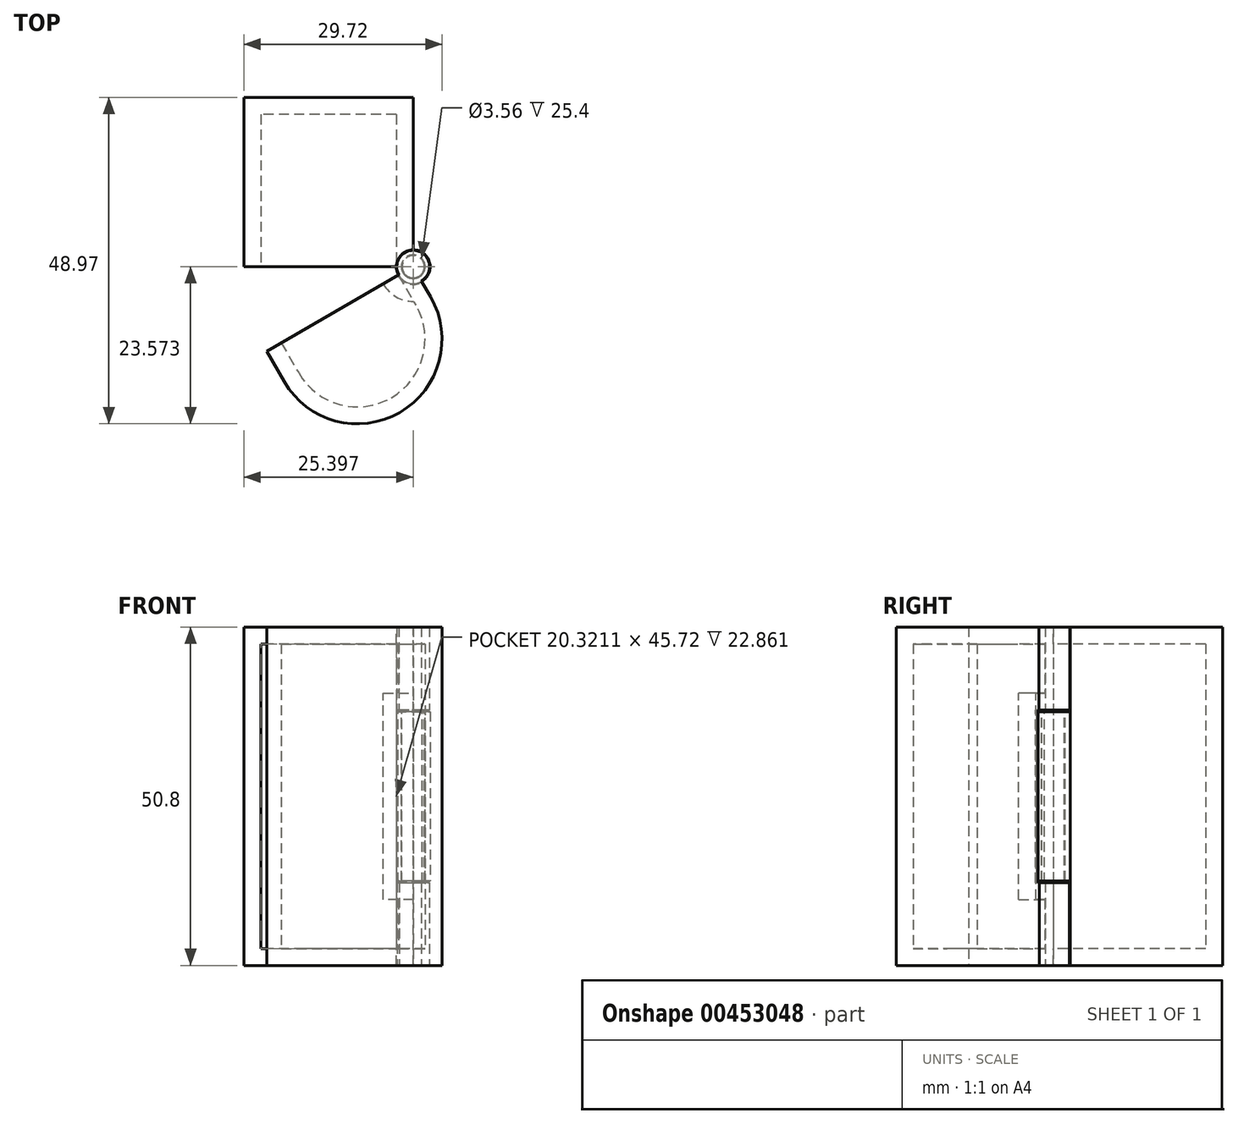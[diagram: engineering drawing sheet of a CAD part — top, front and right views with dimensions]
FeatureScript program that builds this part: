
annotation { "Feature Type Name" : "Feature", "Feature Type Description" : "" }
export const myFeature = defineFeature(function(context is Context, id is Id, definition is map)
    precondition{}
    {
        {
            var Q0;
            Q0=qCreatedBy(makeId("Top.planeOp"),FACE);
            var sketch = newSketch(context, id + "F0", { "sketchPlane" : qUnion([Q0])});
            skLineSegment(sketch, "E0.bottom", {"start": v(-18.17, 30.36) * mm, "end": v(-43.57, 30.36) * mm});
            skLineSegment(sketch, "E0.top", {"start": v(-18.17, 4.96) * mm, "end": v(-43.57, 4.96) * mm});
            skLineSegment(sketch, "E0.left", {"start": v(-18.17, 30.36) * mm, "end": v(-18.17, 4.96) * mm});
            skLineSegment(sketch, "E0.right", {"start": v(-43.57, 30.36) * mm, "end": v(-43.57, 4.96) * mm});
            skSolve(sketch);
        }
        {
            var Q0;
            Q0=makeQuery(id+"F0.imprint","IMPRINT",FACE,{"disambiguationData":[TD([[makeQuery(id+"F0.imprint","IMPRINT",EDGE,{"derivedFrom":sQuery(id+"F0.wireOp",EDGE,"E0.bottom")}),1.0]])]});
            extrude(context, id + "F1", {"entities" : qUnion([Q0]), "depth" : 50.8 * mm});
        }
        {
            var Q0;
            Q0=makeQuery(id+"F1.opExtrude","SWEPT_FACE",FACE,{"disambiguationData":[OSD([sQuery(id+"F0.wireOp",EDGE,"E0.top")])]});
            shell(context, id + "F2", {"entities" : qUnion([Q0]), "thickness" : 2.54 * mm});
        }
        {
            var Q0;
            Q0=makeQuery(id+"F1.opExtrude","SWEPT_FACE",FACE,{"disambiguationData":[OSD([sQuery(id+"F0.wireOp",EDGE,"E0.top")])]});
            var sketch = newSketch(context, id + "F3", { "sketchPlane" : qUnion([Q0])});
            skLineSegment(sketch, "E1", {"start": v(-20.71, 48.26) * mm, "end": v(-20.71, 50.8) * mm});
            skLineSegment(sketch, "E2", {"start": v(-20.71, 50.8) * mm, "end": v(-20.71, 0) * mm});
            skSolve(sketch);
        }
        {
            var Q0;
            {var subQ0=sQuery(id+"F0.wireOp",EDGE,"E0.top");var subQ1=makeQuery(id+"F1.opExtrude","SWEPT_EDGE",EDGE,{"disambiguationData":[OSD([subQ0,sQuery(id+"F0.wireOp",EDGE,"E0.left")])]});Q0=makeQuery(id+"F3.imprint","IMPRINT",FACE,{"disambiguationData":[TD([[makeQuery(id+"F3.imprint","IMPRINT",EDGE,{"derivedFrom":subQ1}),-1.0]])]});}
            var Q1;
            Q1=makeQuery(id+"F1.opExtrude","SWEPT_EDGE",EDGE,{"disambiguationData":[OSD([sQuery(id+"F0.wireOp",EDGE,"E0.top"),sQuery(id+"F0.wireOp",EDGE,"E0.left")])]});
            revolve(context, id + "F4", {"operationType" : NewBodyOperationType.ADD, "entities" : qUnion([Q0]), "axis" : qUnion([Q1]), "revolveType" : RevolveType.ONE_DIRECTION, "oppositeDirection" : true, "angle" : 270 * degree});
        }
        {
            var Q0;
            {var subQ0=sQuery(id+"F0.wireOp",EDGE,"E0.top");var subQ1=makeQuery(id+"F1.opExtrude","CAP_EDGE",EDGE,{"disambiguationData":[OSD([subQ0])],"isStart":false});var subQ2=sQuery(id+"F0.wireOp",EDGE,"E0.left");Q0=makeQuery(id+"F4.boolean.opBoolean","MERGE",FACE,{"derivedFrom":[makeQuery(id+"F1.opExtrude","CAP_FACE",FACE,{"disambiguationData":[OSD([sQuery(id+"F0.wireOp",EDGE,"E0.bottom"),subQ0,subQ2,sQuery(id+"F0.wireOp",EDGE,"E0.right")])],"isStart":false}),makeQuery(id+"F4.opRevolve","SWEPT_FACE",FACE,{"disambiguationData":[OSD([subQ0]),TDD([makeQuery(id+"F3.imprint","IMPRINT",EDGE,{"disambiguationData":[TD([[makeQuery(id+"F3.imprint","INTERSECT",VERTEX,{"derivedFrom":[subQ1,sQuery(id+"F3.wireOp",EDGE,"E2")]}),1.0]])],"derivedFrom":subQ1})])]})]});}
            var sketch = newSketch(context, id + "F5", { "sketchPlane" : qUnion([Q0])});
            skCircle(sketch, "E3", {"center": v(-18.17, 4.96) * mm, "radius": 2.54 * mm});
            skSolve(sketch);
        }
        {
            var Q0;
            {var subQ0=sQuery(id+"F0.wireOp",EDGE,"E0.top");var subQ1=makeQuery(id+"F1.opExtrude","CAP_EDGE",EDGE,{"disambiguationData":[OSD([subQ0])],"isStart":true});var subQ2=sQuery(id+"F0.wireOp",EDGE,"E0.left");Q0=makeQuery(id+"F4.boolean.opBoolean","MERGE",FACE,{"derivedFrom":[makeQuery(id+"F1.opExtrude","CAP_FACE",FACE,{"disambiguationData":[OSD([sQuery(id+"F0.wireOp",EDGE,"E0.bottom"),subQ0,subQ2,sQuery(id+"F0.wireOp",EDGE,"E0.right")])],"isStart":true}),makeQuery(id+"F4.opRevolve","SWEPT_FACE",FACE,{"disambiguationData":[OSD([subQ0]),TDD([makeQuery(id+"F3.imprint","IMPRINT",EDGE,{"disambiguationData":[TD([[makeQuery(id+"F3.imprint","INTERSECT",VERTEX,{"derivedFrom":[subQ1,sQuery(id+"F3.wireOp",EDGE,"E2")]}),1.0]])],"derivedFrom":subQ1})])]})]});}
            var sketch = newSketch(context, id + "F6", { "sketchPlane" : qUnion([Q0])});
            skCircle(sketch, "E4", {"center": v(-18.17, -4.96) * mm, "radius": 2.54 * mm});
            skSolve(sketch);
        }
        {
            var Q0;
            {var subQ0=sQuery(id+"F6.wireOp",EDGE,"E4");var subQ1=makeQuery(id+"F6.imprint","INTERSECT",VERTEX,{"derivedFrom":[makeQuery(id+"F1.opExtrude","CAP_EDGE",EDGE,{"disambiguationData":[OSD([sQuery(id+"F0.wireOp",EDGE,"E0.top")])],"isStart":true}),subQ0]});Q0=makeQuery(id+"F6.imprint","IMPRINT",FACE,{"disambiguationData":[TD([[makeQuery(id+"F6.imprint","IMPRINT",EDGE,{"disambiguationData":[TD([[subQ1,1.0]])],"derivedFrom":subQ0}),1.0]])]});}
            extrude(context, id + "F7", {"entities" : qUnion([Q0]), "operationType" : NewBodyOperationType.REMOVE, "oppositeDirection" : true, "depth" : 12.7 * mm});
        }
        {
            var Q0;
            {var subQ0=sQuery(id+"F5.wireOp",EDGE,"E3");Q0=makeQuery(id+"F5.imprint","IMPRINT",FACE,{"disambiguationData":[TD([[makeQuery(id+"F5.imprint","IMPRINT",EDGE,{"disambiguationData":[OD(0.0)],"derivedFrom":subQ0}),1.0]])]});}
            var sketch = newSketch(context, id + "F8", { "sketchPlane" : qUnion([Q0])});
            skArc(sketch, "E5.0", {"start": v(-19.95, 4.96) * mm, "mid": v(-16.92, 3.7) * mm, "end": v(-18.17, 6.74) * mm});
            skArc(sketch, "E5.1", {"start": v(-18.17, 6.74) * mm, "mid": v(-19.43, 6.22) * mm, "end": v(-19.95, 4.96) * mm});
            skSolve(sketch);
        }
        {
            var Q0;
            Q0=makeQuery(id+"F8.imprint","IMPRINT",FACE,{"disambiguationData":[TD([[makeQuery(id+"F8.imprint","IMPRINT",EDGE,{"derivedFrom":sQuery(id+"F8.wireOp",EDGE,"E5.0")}),1.0]])]});
            extrude(context, id + "F9", {"entities" : qUnion([Q0]), "operationType" : NewBodyOperationType.REMOVE, "endBound" : BoundingType.UP_TO_NEXT, "oppositeDirection" : true, "depth" : 25.4 * mm});
        }
        {
            var Q0;
            {var subQ0=sQuery(id+"F5.wireOp",EDGE,"E3");Q0=makeQuery(id+"F5.imprint","IMPRINT",FACE,{"disambiguationData":[TD([[makeQuery(id+"F5.imprint","IMPRINT",EDGE,{"disambiguationData":[OD(0.0)],"derivedFrom":subQ0}),1.0]])]});}
            extrude(context, id + "F10", {"entities" : qUnion([Q0]), "operationType" : NewBodyOperationType.REMOVE, "oppositeDirection" : true, "depth" : 12.7 * mm});
        }
        {
            var Q0;
            Q0=qCreatedBy(makeId("Top.planeOp"),FACE);
            var sketch = newSketch(context, id + "F11", { "sketchPlane" : qUnion([Q0])});
            skLineSegment(sketch, "E6.bottom", {"start": v(-43.63, 4.5) * mm, "end": v(-18.25, 4.5) * mm});
            skLineSegment(sketch, "E6.top", {"start": v(-43.63, -13.44) * mm, "end": v(-18.25, -13.44) * mm});
            skLineSegment(sketch, "E6.left", {"start": v(-43.63, 4.5) * mm, "end": v(-43.63, -13.44) * mm});
            skLineSegment(sketch, "E6.right", {"start": v(-18.25, 4.5) * mm, "end": v(-18.25, -13.44) * mm});
            skSolve(sketch);
        }
        {
            var Q0;
            Q0=makeQuery(id+"F11.imprint","IMPRINT",FACE,{"disambiguationData":[TD([[makeQuery(id+"F11.imprint","IMPRINT",EDGE,{"derivedFrom":sQuery(id+"F11.wireOp",EDGE,"E6.bottom")}),-1.0]])]});
            extrude(context, id + "F12", {"entities" : qUnion([Q0]), "depth" : 12.45 * mm});
        }
        {
            var Q0;
            Q0=makeQuery(id+"F12.opExtrude","SWEPT_BODY",BODY,{"disambiguationData":[OSD([sQuery(id+"F11.wireOp",EDGE,"E6.bottom"),sQuery(id+"F11.wireOp",EDGE,"E6.top"),sQuery(id+"F11.wireOp",EDGE,"E6.left"),sQuery(id+"F11.wireOp",EDGE,"E6.right")])]});
            var Q1;
            Q1=makeQuery(id+"F12.opExtrude","SWEPT_EDGE",EDGE,{"disambiguationData":[OSD([sQuery(id+"F11.wireOp",EDGE,"E6.top"),sQuery(id+"F11.wireOp",EDGE,"E6.right")])]});
            transform(context, id + "F13", {"entities" : qUnion([Q0]), "transformType" : TransformType.ROTATION, "transformAxis" : qUnion([Q1]), "angle" : 30 * degree, "oppositeDirection" : true, "makeCopy" : false});
        }
        {
            var Q0;
            Q0=makeQuery(id+"F12.opExtrude","SWEPT_BODY",BODY,{"disambiguationData":[OSD([sQuery(id+"F11.wireOp",EDGE,"E6.bottom"),sQuery(id+"F11.wireOp",EDGE,"E6.top"),sQuery(id+"F11.wireOp",EDGE,"E6.left"),sQuery(id+"F11.wireOp",EDGE,"E6.right")])]});
            var Q1;
            Q1=makeQuery(id+"F12.opExtrude","CAP_VERTEX",VERTEX,{"disambiguationData":[OSD([sQuery(id+"F11.wireOp",EDGE,"E6.bottom"),sQuery(id+"F11.wireOp",EDGE,"E6.right")])],"isStart":false});
            var Q2;
            Q2=sQuery(id+"F5.wireOp",VERTEX,"E3.center");
            transform(context, id + "F14", {"entities" : qUnion([Q0]), "transformType" : TransformType.TRANSLATION_ENTITY, "oppositeDirectionEntity" : false, "transformLine" : qUnion([Q1, Q2]), "makeCopy" : false});
        }
        {
            var Q0;
            Q0=makeQuery(id+"F12.opExtrude","SWEPT_FACE",FACE,{"disambiguationData":[OSD([sQuery(id+"F11.wireOp",EDGE,"E6.right")])]});
            var sketch = newSketch(context, id + "F15", { "sketchPlane" : qUnion([Q0])});
            skLineSegment(sketch, "E7", {"start": v(10.93, 50.8) * mm, "end": v(10.93, 38.35) * mm});
            skSolve(sketch);
        }
        {
            var Q0;
            {var subQ0=sQuery(id+"F15.wireOp",EDGE,"E7");Q0=makeQuery(id+"F15.imprint","IMPRINT",FACE,{"disambiguationData":[TD([[makeQuery(id+"F15.imprint","IMPRINT",EDGE,{"derivedFrom":subQ0}),1.0]])]});}
            var Q1;
            Q1=makeQuery(id+"F12.opExtrude","SWEPT_EDGE",EDGE,{"disambiguationData":[OSD([sQuery(id+"F11.wireOp",EDGE,"E6.bottom"),sQuery(id+"F11.wireOp",EDGE,"E6.right")])]});
            revolve(context, id + "F16", {"operationType" : NewBodyOperationType.ADD, "entities" : qUnion([Q0]), "axis" : qUnion([Q1]), "revolveType" : RevolveType.ONE_DIRECTION, "oppositeDirection" : true, "angle" : 270 * degree});
        }
        {
            var Q0;
            {var subQ0=sQuery(id+"F11.wireOp",EDGE,"E6.right");var subQ1=makeQuery(id+"F12.opExtrude","CAP_EDGE",EDGE,{"disambiguationData":[OSD([subQ0])],"isStart":true});var subQ2=sQuery(id+"F11.wireOp",EDGE,"E6.bottom");Q0=makeQuery(id+"F16.boolean.opBoolean","MERGE",FACE,{"derivedFrom":[makeQuery(id+"F12.opExtrude","CAP_FACE",FACE,{"disambiguationData":[OSD([subQ2,sQuery(id+"F11.wireOp",EDGE,"E6.top"),sQuery(id+"F11.wireOp",EDGE,"E6.left"),subQ0])],"isStart":true}),makeQuery(id+"F16.opRevolve","SWEPT_FACE",FACE,{"disambiguationData":[OSD([subQ0]),TDD([makeQuery(id+"F15.imprint","IMPRINT",EDGE,{"disambiguationData":[TD([[makeQuery(id+"F15.imprint","INTERSECT",VERTEX,{"derivedFrom":[subQ1,sQuery(id+"F15.wireOp",EDGE,"E7")]}),1.0]])],"derivedFrom":subQ1})])]})]});}
            var sketch = newSketch(context, id + "F17", { "sketchPlane" : qUnion([Q0])});
            skCircle(sketch, "E8", {"center": v(-18.17, -4.96) * mm, "radius": 2.66 * mm});
            skSolve(sketch);
        }
        {
            var Q0;
            {var subQ1=makeQuery(id+"F12.opExtrude","CAP_EDGE",EDGE,{"disambiguationData":[OSD([sQuery(id+"F11.wireOp",EDGE,"E6.top")])],"isStart":true});Q0=makeQuery(id+"F17.imprint","IMPRINT",FACE,{"disambiguationData":[TD([[makeQuery(id+"F17.imprint","IMPRINT",EDGE,{"derivedFrom":subQ1}),-1.0]])]});}
            extrude(context, id + "F18", {"entities" : qUnion([Q0]), "operationType" : NewBodyOperationType.ADD, "depth" : 38.35 * mm});
        }
        {
            var Q0;
            {var subQ0=sQuery(id+"F11.wireOp",EDGE,"E6.right");var subQ1=makeQuery(id+"F12.opExtrude","CAP_EDGE",EDGE,{"disambiguationData":[OSD([subQ0])],"isStart":true});var subQ2=sQuery(id+"F11.wireOp",EDGE,"E6.bottom");Q0=makeQuery(id+"F16.boolean.opBoolean","MERGE",FACE,{"derivedFrom":[makeQuery(id+"F12.opExtrude","CAP_FACE",FACE,{"disambiguationData":[OSD([subQ2,sQuery(id+"F11.wireOp",EDGE,"E6.top"),sQuery(id+"F11.wireOp",EDGE,"E6.left"),subQ0])],"isStart":true}),makeQuery(id+"F16.opRevolve","SWEPT_FACE",FACE,{"disambiguationData":[OSD([subQ0]),TDD([makeQuery(id+"F15.imprint","IMPRINT",EDGE,{"disambiguationData":[TD([[makeQuery(id+"F15.imprint","INTERSECT",VERTEX,{"derivedFrom":[subQ1,sQuery(id+"F15.wireOp",EDGE,"E7")]}),1.0]])],"derivedFrom":subQ1})])]})]});}
            var sketch = newSketch(context, id + "F19", { "sketchPlane" : qUnion([Q0])});
            skCircle(sketch, "E9", {"center": v(-18.17, -4.96) * mm, "radius": 1.68 * mm});
            skSolve(sketch);
        }
        {
            var Q0;
            Q0=makeQuery(id+"F19.imprint","IMPRINT",FACE,{"disambiguationData":[TD([[makeQuery(id+"F19.imprint","IMPRINT",EDGE,{"derivedFrom":sQuery(id+"F19.wireOp",EDGE,"E9")}),1.0]])]});
            extrude(context, id + "F20", {"entities" : qUnion([Q0]), "operationType" : NewBodyOperationType.ADD, "depth" : 38.35 * mm});
        }
        {
            var Q0;
            Q0=makeQuery(id+"F20.opExtrude","CAP_FACE",FACE,{"disambiguationData":[OSD([sQuery(id+"F19.wireOp",EDGE,"E9")])],"isStart":false});
            var sketch = newSketch(context, id + "F21", { "sketchPlane" : qUnion([Q0])});
            skCircle(sketch, "E10", {"center": v(-18.17, -4.96) * mm, "radius": 2.4 * mm});
            skSolve(sketch);
        }
        {
            var Q0;
            Q0=makeQuery(id+"F18.opExtrude","CAP_FACE",FACE,{"disambiguationData":[OSD([sQuery(id+"F11.wireOp",EDGE,"E6.bottom"),sQuery(id+"F11.wireOp",EDGE,"E6.top"),sQuery(id+"F11.wireOp",EDGE,"E6.left"),sQuery(id+"F11.wireOp",EDGE,"E6.right"),sQuery(id+"F17.wireOp",EDGE,"E8")])],"isStart":false});
            var sketch = newSketch(context, id + "F22", { "sketchPlane" : qUnion([Q0])});
            skLineSegment(sketch, "E11", {"start": v(-16.84, -2.66) * mm, "end": v(-18.17, -4.96) * mm});
            skLineSegment(sketch, "E12", {"start": v(-18.17, -4.96) * mm, "end": v(-20.47, -3.63) * mm});
            skSolve(sketch);
        }
        {
            var Q0;
            Q0=makeQuery(id+"F21.imprint","IMPRINT",FACE,{"disambiguationData":[TD([[makeQuery(id+"F21.imprint","IMPRINT",EDGE,{"derivedFrom":sQuery(id+"F21.wireOp",EDGE,"E10")}),1.0]])]});
            var Q1;
            Q1=makeQuery(id+"F22.imprint","IMPRINT",FACE,{"disambiguationData":[TD([[makeQuery(id+"F22.imprint","IMPRINT",EDGE,{"derivedFrom":sQuery(id+"F22.wireOp",EDGE,"E11")}),-1.0]])]});
            extrude(context, id + "F23", {"entities" : qUnion([Q0, Q1]), "operationType" : NewBodyOperationType.ADD, "oppositeDirection" : true, "depth" : 12.45 * mm});
        }
        {
            var Q0;
            {var subQ0=sQuery(id+"F11.wireOp",EDGE,"E6.left");var subQ1=sQuery(id+"F11.wireOp",EDGE,"E6.top");Q0=makeQuery(id+"F18.boolean.opBoolean","MERGE",EDGE,{"derivedFrom":[makeQuery(id+"F12.opExtrude","SWEPT_EDGE",EDGE,{"disambiguationData":[OSD([subQ1,subQ0])]}),makeQuery(id+"F18.opExtrude","SWEPT_EDGE",EDGE,{"disambiguationData":[OSD([subQ1,subQ0])]})]});}
            fillet(context, id + "F24", {"entities" : qUnion([Q0]), "radius" : 12.7 * mm, "tangentPropagation" : true, "allowEdgeOverflow" : false});
        }
        {
            var Q0;
            {var subQ0=sQuery(id+"F11.wireOp",EDGE,"E6.right");var subQ1=sQuery(id+"F11.wireOp",EDGE,"E6.top");Q0=makeQuery(id+"F18.boolean.opBoolean","MERGE",EDGE,{"derivedFrom":[makeQuery(id+"F12.opExtrude","SWEPT_EDGE",EDGE,{"disambiguationData":[OSD([subQ1,subQ0])]}),makeQuery(id+"F18.opExtrude","SWEPT_EDGE",EDGE,{"disambiguationData":[OSD([subQ1,subQ0])]})]});}
            fillet(context, id + "F25", {"entities" : qUnion([Q0]), "radius" : 12.7 * mm, "tangentPropagation" : true, "allowEdgeOverflow" : false});
        }
        {
            var Q0;
            {var subQ0=sQuery(id+"F11.wireOp",EDGE,"E6.bottom");Q0=makeQuery(id+"F23.boolean.opBoolean","MERGE",FACE,{"derivedFrom":[makeQuery(id+"F18.boolean.opBoolean","MERGE",FACE,{"derivedFrom":[makeQuery(id+"F12.opExtrude","SWEPT_FACE",FACE,{"disambiguationData":[OSD([subQ0])]}),makeQuery(id+"F18.opExtrude","SWEPT_FACE",FACE,{"disambiguationData":[OSD([subQ0])]})]}),makeQuery(id+"F23.opExtrude","SWEPT_FACE",FACE,{"disambiguationData":[OSD([sQuery(id+"F22.wireOp",EDGE,"E12")])]})]});}
            shell(context, id + "F26", {"entities" : qUnion([Q0]), "thickness" : 2.54 * mm});
        }
    });
